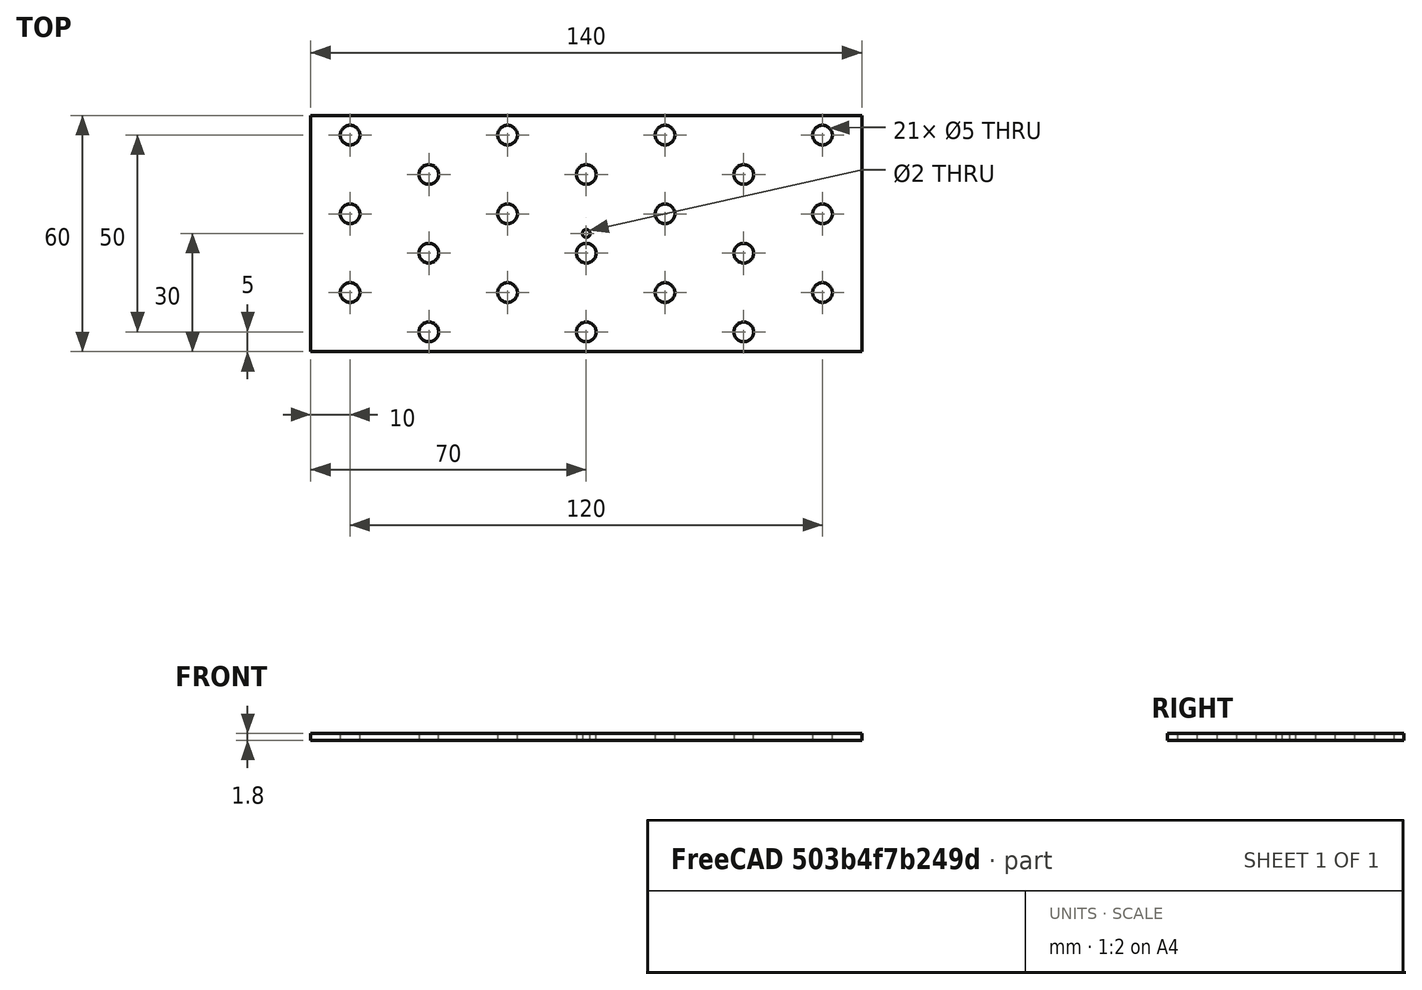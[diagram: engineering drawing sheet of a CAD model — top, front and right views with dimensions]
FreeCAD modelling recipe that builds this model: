
FCSTD DOCUMENT  (FreeCAD 0.19R24276 (Git))
Label: Bar_60x140__1_8mm
License: All rights reserved
LicenseURL: http://en.wikipedia.org/wiki/All_rights_reserved
objects: Sketcher::SketchObject×1, PartDesign::Pad×1, PartDesign::Body×1
note: 4 computed .brp shape members not serialized (recipe doc carries the construction recipe); baked Part::Feature solids carry a one-line shape summary decoded from their .brp

FEATURE [Sketcher::SketchObject] Sketch
  FullyConstrained = false
  MapMode = 5
  Support = -> [XY_Plane]
  sketch-geometry (48):
    g0: LineSegment StartX=0 StartY=0 StartZ=0 EndX=120 EndY=0 EndZ=0
    g1: LineSegment StartX=120 StartY=0 StartZ=0 EndX=120 EndY=80 EndZ=0
    g2: LineSegment StartX=120 StartY=80 StartZ=0 EndX=0 EndY=80 EndZ=0
    g3: LineSegment StartX=0 StartY=80 StartZ=0 EndX=0 EndY=0 EndZ=0
    g4: LineSegment StartX=0 StartY=4.5 StartZ=0 EndX=120 EndY=4.5 EndZ=0
    g5: LineSegment StartX=0 StartY=24.5 StartZ=0 EndX=120 EndY=24.5 EndZ=0
    g6: LineSegment StartX=0 StartY=44.5 StartZ=0 EndX=120 EndY=44.5 EndZ=0
    g7: LineSegment StartX=0 StartY=64.5 StartZ=0 EndX=120 EndY=64.5 EndZ=0
    g8: LineSegment StartX=48.5 StartY=0 StartZ=0 EndX=48.5 EndY=4.5 EndZ=0
    g9: LineSegment StartX=68.5 StartY=0 StartZ=0 EndX=68.5 EndY=4.5 EndZ=0
    g10: LineSegment StartX=88.5 StartY=0 StartZ=0 EndX=88.5 EndY=4.5 EndZ=0
    g11: LineSegment StartX=108.5 StartY=0 StartZ=0 EndX=108.5 EndY=4.5 EndZ=0
    g12: LineSegment StartX=0 StartY=14.5 StartZ=0 EndX=120 EndY=14.5 EndZ=0
    g13: LineSegment StartX=0 StartY=34.5 StartZ=0 EndX=120 EndY=34.5 EndZ=0
    g14: LineSegment StartX=0 StartY=54.5 StartZ=0 EndX=120 EndY=54.5 EndZ=0
    g15: LineSegment StartX=0 StartY=74.5 StartZ=0 EndX=120 EndY=74.5 EndZ=0
    g16: LineSegment StartX=48.5 StartY=24.5 StartZ=0 EndX=48.5 EndY=80 EndZ=0
    g17: LineSegment StartX=68.5 StartY=14.5 StartZ=0 EndX=68.5 EndY=80 EndZ=0
    g18: LineSegment StartX=88.5 StartY=24.5 StartZ=0 EndX=88.5 EndY=80 EndZ=0
    g19: LineSegment StartX=108.5 StartY=14.5 StartZ=0 EndX=108.5 EndY=80 EndZ=0
    g20: Circle CenterX=28.5 CenterY=14.5 CenterZ=0 NormalX=0 NormalY=0 NormalZ=1 AngleXU=0 Radius=2.5
    g21: Circle CenterX=108.5 CenterY=14.5 CenterZ=0 NormalX=0 NormalY=0 NormalZ=1 AngleXU=0 Radius=2.5
    g22: Circle CenterX=8.5 CenterY=24.5 CenterZ=0 NormalX=0 NormalY=0 NormalZ=1 AngleXU=0 Radius=2.5
    g23: Circle CenterX=48.5 CenterY=24.5 CenterZ=0 NormalX=0 NormalY=0 NormalZ=1 AngleXU=0 Radius=2.5
    g24: Circle CenterX=88.5 CenterY=24.5 CenterZ=0 NormalX=0 NormalY=0 NormalZ=1 AngleXU=0 Radius=2.5
    g25: Circle CenterX=8.5 CenterY=44.5 CenterZ=0 NormalX=0 NormalY=0 NormalZ=1 AngleXU=0 Radius=2.5
    g26: Circle CenterX=48.5 CenterY=44.5 CenterZ=0 NormalX=0 NormalY=0 NormalZ=1 AngleXU=0 Radius=2.5
    g27: Circle CenterX=88.5 CenterY=44.5 CenterZ=0 NormalX=0 NormalY=0 NormalZ=1 AngleXU=0 Radius=2.5
    g28: Circle CenterX=28.5 CenterY=54.5 CenterZ=0 NormalX=0 NormalY=0 NormalZ=1 AngleXU=0 Radius=2.5
    g29: Circle CenterX=68.5 CenterY=54.5 CenterZ=0 NormalX=0 NormalY=0 NormalZ=1 AngleXU=0 Radius=2.5
    g30: Circle CenterX=108.5 CenterY=54.5 CenterZ=0 NormalX=0 NormalY=0 NormalZ=1 AngleXU=0 Radius=2.5
    g31: Circle CenterX=88.5 CenterY=64.5 CenterZ=0 NormalX=0 NormalY=0 NormalZ=1 AngleXU=0 Radius=2.5
    g32: Circle CenterX=48.5 CenterY=64.5 CenterZ=0 NormalX=0 NormalY=0 NormalZ=1 AngleXU=0 Radius=2.5
    g33: Circle CenterX=8.5 CenterY=64.5 CenterZ=0 NormalX=0 NormalY=0 NormalZ=1 AngleXU=0 Radius=2.5
    g34: Circle CenterX=28.5 CenterY=34.5 CenterZ=0 NormalX=0 NormalY=0 NormalZ=1 AngleXU=0 Radius=2.5
    g35: Circle CenterX=68.5 CenterY=34.5 CenterZ=0 NormalX=0 NormalY=0 NormalZ=1 AngleXU=0 Radius=2.5
    g36: Circle CenterX=108.5 CenterY=34.5 CenterZ=0 NormalX=0 NormalY=0 NormalZ=1 AngleXU=0 Radius=2.5
    g37: LineSegment StartX=28.5 StartY=74.5 StartZ=0 EndX=28.5 EndY=14.5 EndZ=0
    g38: LineSegment StartX=8.5 StartY=4.5 StartZ=0 EndX=8.5 EndY=24.5 EndZ=0
    g39: Circle CenterX=68.5 CenterY=14.5 CenterZ=0 NormalX=0 NormalY=0 NormalZ=1 AngleXU=0 Radius=2.5
    g40: LineSegment StartX=-1.5 StartY=9.5 StartZ=0 EndX=138.5 EndY=9.5 EndZ=0
    g41: LineSegment StartX=-1.5 StartY=69.5 StartZ=0 EndX=138.5 EndY=69.5 EndZ=0
    g42: LineSegment StartX=-1.5 StartY=69.5 StartZ=0 EndX=-1.5 EndY=9.5 EndZ=0
    g43: LineSegment StartX=138.5 StartY=69.5 StartZ=0 EndX=138.5 EndY=9.5 EndZ=0
    g44: Circle CenterX=128.5 CenterY=24.5 CenterZ=0 NormalX=0 NormalY=0 NormalZ=1 AngleXU=0 Radius=2.5
    g45: Circle CenterX=128.5 CenterY=44.5 CenterZ=0 NormalX=0 NormalY=0 NormalZ=1 AngleXU=0 Radius=2.5
    g46: Circle CenterX=128.5 CenterY=64.5 CenterZ=0 NormalX=0 NormalY=0 NormalZ=1 AngleXU=0 Radius=2.5
    g47: Circle CenterX=68.5 CenterY=39.5 CenterZ=0 NormalX=0 NormalY=0 NormalZ=1 AngleXU=0 Radius=1
  constraints (102):
    c: Coincident(g0,g1)
    c: Coincident(g1,g2)
    c: Coincident(g2,g3)
    c: Coincident(g3,g0)
    c: Horizontal(g0)
    c: Horizontal(g2)
    c: Vertical(g1)
    c: Vertical(g3)
    c: Coincident(g0,g-1)
    c: DistanceX(g0,g0) = 120
    c: DistanceY(g3,g3) = 80
    c: Horizontal(g4)
    c: PointOnObject(g4,g3)
    c: PointOnObject(g4,g1)
    c: Horizontal(g5)
    c: PointOnObject(g5,g3)
    c: PointOnObject(g5,g1)
    c: DistanceY(g4,g5) = 20
    c: Horizontal(g6)
    c: PointOnObject(g6,g1)
    c: PointOnObject(g6,g3)
    c: DistanceY(g5,g6) = 20
    c: Horizontal(g7)
    c: PointOnObject(g7,g1)
    c: PointOnObject(g7,g3)
    c: DistanceY(g6,g7) = 20
    c: Vertical(g8)
    c: Vertical(g9)
    c: Vertical(g10)
    c: Vertical(g11)
    c: PointOnObject(g8,g0)
    c: PointOnObject(g9,g0)
    c: PointOnObject(g10,g0)
    c: PointOnObject(g11,g0)
    c: PointOnObject(g19,g2)
    c: PointOnObject(g18,g2)
    c: PointOnObject(g17,g2)
    c: PointOnObject(g16,g2)
    c: DistanceX(g8,g9) = 20
    c: DistanceX(g9,g10) = 20
    c: DistanceX(g10,g11) = 20
    c: Horizontal(g12)
    c: Horizontal(g13)
    c: Horizontal(g14)
    c: Horizontal(g15)
    c: PointOnObject(g12,g3)
    c: PointOnObject(g13,g3)
    c: PointOnObject(g14,g3)
    c: PointOnObject(g15,g3)
    c: PointOnObject(g15,g1)
    c: PointOnObject(g14,g1)
    c: PointOnObject(g13,g1)
    c: PointOnObject(g12,g1)
    c: DistanceY(g0,g12) = 14.5
    c: DistanceY(g12,g13) = 20
    c: DistanceY(g13,g14) = 20
    c: DistanceY(g14,g15) = 20
    c: PointOnObject(g20,g12)
    c: PointOnObject(g8,g4)
    c: Tangent(g8,g16)
    c: PointOnObject(g9,g4)
    c: PointOnObject(g17,g12)
    c: Tangent(g9,g17)
    c: PointOnObject(g10,g4)
    c: Tangent(g10,g18)
    c: PointOnObject(g11,g4)
    c: PointOnObject(g19,g12)
    c: Tangent(g11,g19)
    c: Coincident(g21,g19)
    c: Diameter(g20) = 5
    c: PointOnObject(g16,g5)
    c: PointOnObject(g18,g5)
    c: Equal(g23,g24)
    c: Equal(g33,g28)
    c: Equal(g28,g32)
    c: Equal(g32,g31)
    c: Equal(g31,g30)
    c: Diameter(g28) = 5
    c: Equal(g31,g29)
    c: Equal(g26,g27)
    c: Diameter(g34) = 5
    c: Coincident(g37,g20)
    c: Vertical(g37)
    c: DistanceY(g0,g4) = 4.5
    c: Coincident(g38,g22)
    c: Vertical(g38)
    c: Coincident(g39,g17)
    c: Equal(g21,g39)
    c: Horizontal(g40)
    c: Horizontal(g41)
    c: Vertical(g42)
    c: DistanceX(g0,g38) = 8.5
    c: Coincident(g42,g40)
    c: Coincident(g41,g42)
    c: Vertical(g43)
    c: DistanceX(g40,g38) = 10
    c: Coincident(g40,g43)
    c: DistanceY(g40,g21) = 5
    c: Coincident(g41,g43)
    c: DistanceY(g40,g41) = 60
    c: DistanceX(g41,g41) = 140
    c: Diameter(g47) = 2
FEATURE [PartDesign::Pad] Pad
  Direction = (1,1,1)
  Length = 1.8
  Length2 = 100
  Profile = -> Sketch
  Type = 0
FEATURE [PartDesign::Body] Body
  Group = -> [Sketch,Pad]
  Origin = -> Origin
  Tip = -> Pad
